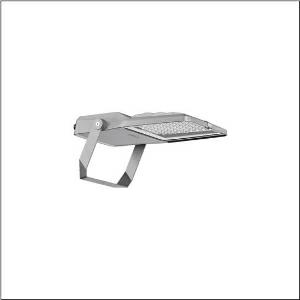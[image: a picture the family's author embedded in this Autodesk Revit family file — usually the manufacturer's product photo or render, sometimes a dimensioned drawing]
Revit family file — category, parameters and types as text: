
# Revit family: floodlight_fl_21_iq_mini___pl52_5xa7772d2d1a_b3d3
name_source: partatom
category: Lighting Fixtures
units: mm (PartAtom-declared; Revit-internal decimal feet)

## family parameters
Cut with Voids When Loaded = No
Host = Face
Light Source = No
Part Type = Normal
Room Calculation Point = No
Round Connector Dimension = Use Diameter
Shared = No

## types (1)
- --- (1 x LED, 17830 lm, 143 W, 3000K)
    Apparent Load = 143 VA
    CIE Flux Codes = 26 60 98 100 100
    Color Rendering = 70
    Color Temperature = 3000K
    Default Elevation = 1800 mm
    Description = Floodlight FL 21 iQ mini, floodlight, primary light control with lens, of PMMA, primary optical cover: protective disc, of toughened safety glass, transparent, light distribution: PL52, light emission: direct distribution, installation type: surface-mounted, LED, High Power LED, rated luminous flux: 17.830lm, luminous efficacy: 125lm/W, light colour: 730, colour temperature: 3000K, control gear: iQ Street-Remote/DALI, control: Street-Remote, Auto-Match, Temp-Guard, Night-Set, Smart-Wire, Desk-Remote (wireless, voltage-free reading and setting of iQ features in the workshop via application-optimized NFC function/RFID function), optimised constant luminous flux control (CLO 2.0), with terminal, 6-pole, mains connection: 220..240V, AC, 50/60Hz, start of lifetime: 143W, end of service life: 152W, reduction: 61W, luminaire housing, of diecast aluminium, powder-coated, Siteco® metallic grey (DB 702S), corrosivity category C5 mid according to DIN EN ISO 12944, suitable for swimming pools, chlorine-resistant, sealing non-destructively replaceable, mounting bracket, of steel, galvanised, powder-coated, Siteco® metallic grey (DB 702S), protection rating (complete): IP66, insulation class (complete): insulation class II (safety insulation), certification: CE, ENEC, VDE, protection symbol: D, impact resistance: IK08, permissible operating ambient temperature: -40..+40°C, permissible operating ambient temperature for outdoor applications: -40..+50°C, standard: DIN EN 12944, LABS conformity tested according to VDMA 24364:2018-05, packaging unit: 1 piece

Light Distribution: PL52
    Height = 70 mm
    Lamp = 1 x LED
    Lamp Light Flux = 17830 lm
    Lamp Power = 143 W
    Lamp count = 1
    Length = 485 mm
    Luminous efficacy = 125 lm/W
    Manufacturer = Siteco
    ModVariant = No
    Model = 5XA7772D2D1A
    Number of Poles = 1
    OnlyDefault = Yes
    Power Factor = 1
    Product Name = Floodlight FL 21 iQ mini | PL52
    Product group = floodlight | pylon annexe
    ProductGroupID = 6200
    Protection Class = Protection class II
    Protection Degree = IP 66
    RLX_Detail_Level = 1
    RLX_Emergency_Light_Flux = 0 lm
    RLX_Emergency_Type = 0
    RLX_Emergency_Type_DB = No
    RlxData = <blob elided: 96933 chars, md5=1cf77b25>
    Socket = socket
    Standby Power = 0 W
    System Light Flux = 17830 lm
    System Power = 143 W
    Type Comments = factory setting: luminous flux: 100 % | dim-lin: 254 | 730 mA
    Type Image = l_1006845.jpg
    URL = http://relux.com
    VarID = @adj_163788
    Voltage = 0 V
    Weight = 0.00 kg
    Width = 337 mm

## geometry (parser evidence)
native form markers: Blend x4, Sweep x13
no freeform markers — native parametric forms only
